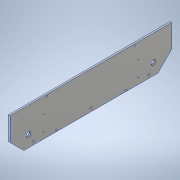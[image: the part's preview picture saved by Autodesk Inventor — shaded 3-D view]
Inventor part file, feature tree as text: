
AUTODESK INVENTOR PART (.ipt)
format: ipt  version: 2021 (Build 250183000, 183)  size: 169,984 bytes
history: native  units: in
note: dims shown in document units (in); Inventor stores cm internally (conversion verified against a paired STEP export)
features: sketch x4, hole x3, chamfer x2, extrude x1, projected_geometry x1
ambient origin geometry x8: Origin, YZ Plane, XZ Plane, XY Plane, X Axis, Y Axis, Z Axis, Center Point
bodies: Solid1 (feature_tree)
feature tree (11):
  extrude  "Extrusion1"  Depth=17.5in
  chamfer  "Chamfer1"  Distance=2.0in
  chamfer  "Chamfer2"  Distance=0.1875in
  hole  "Hole2"  [1 undecoded]
  hole  "Hole3"  [1 undecoded]
  hole  "Hole4"  [1 undecoded]
  sketch  "Sketch1"  dims[d0=4.0in d1=17.5in]
  sketch  "Sketch7"  dims[d2=0.501in]
  projected_geometry  "Projected Loop6"
  sketch  "Sketch9"  dims[d3=1.25in]
  sketch  "Sketch10"  dims[d4=2.0in d5=2.0in d6=0.1875in d7=0.0in d8=1.5in d9=0.125in d10=45.0deg d11=1.5in d12=0.125in d13=45.0deg d22=6.517in d23=0.125in d24=0.603in d25=0.125in d26=0.63in d27=6.517in d28=0.125in d29=0.603in d30=6.517in d31=0.125in d32=0.63in d33=6.517in d95=0.175in d96=0.175in d97=0.175in d98=0.175in d99=4.0in d100=4.0in d101=5.0in d102=5.0in d103=0.15in d104=0.75in d105=0.375in d106=0.25in d107=0.5635in d108=1.0in d109=0.8108in d115=1.7in d116=3.625in d117=3.625in d118=0.65in d119=3.625in d120=3.625in d121=1.7in d122=0.65in d123=0.08in d124=0.198in d125=0.375in d126=0.25in d127=0.5635in d128=0.302in d129=0.8108in d130=0.375in d131=2.5in d132=2.5in d133=12.5in d134=6.25in d135=0.375in d136=0.2in d137=0.5in d138=0.375in d139=0.25in d140=0.5635in d141=0.75in d142=0.8108in]
note: 3 required parameter values undecoded (feature->parameter linkage not recoverable at this tier; creation-order binding heuristic only, values carry confidence <= 0.55)
